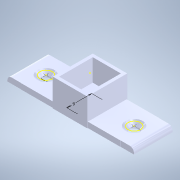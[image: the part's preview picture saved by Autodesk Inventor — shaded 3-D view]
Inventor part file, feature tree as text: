
AUTODESK INVENTOR PART (.ipt)
format: ipt  version: 2021 (Build 250183000, 183)  size: 252,928 bytes
history: mixed  units: in
note: dims shown in document units (in); Inventor stores cm internally (conversion verified against a paired STEP export)
features: sketch x12, extrude x7, hole x2, reference x2, other x2, fillet x1, projected_geometry x1, mirror x1, imported_body x1
ambient origin geometry x8: Origin, YZ Plane, XZ Plane, XY Plane, X Axis, Y Axis, Z Axis, Center Point
bodies: Solid1 (imported_parasolid)
feature tree (29):
  extrude  "Extrusion1"  Depth=0.315in
  sketch  "Sketch2"  dims[d3=0.1339in d4=0.2362in d5=0.248in d6=0.0787in d7=90.0deg d8=0.315in d9=0.0in d14=0.0039in]
  hole  "Hole1"  [1 undecoded]
  sketch  "Sketch4"  dims[d17=0.3937in d18=0.0in d20=0.5512in]
  extrude  "Extrusion3"  Depth=0.5512in
  extrude  "Extrusion4"  Depth=0.3937in TaperAngle=0.0deg
  fillet  "Fillet3"  Radius=0.0591in
  extrude  "Extrusion5"  Depth=0.3937in TaperAngle=0.0deg
  extrude  "Extrusion6"  Depth=0.4921in
  extrude  "Extrusion7"  Depth=0.4803in
  extrude  "Extrusion8"  Depth=0.315in
  sketch  "Sketch12"
  hole  "Hole2"  [1 undecoded]
  sketch  "Sketch1"  dims[d0=0.3937in d1=0.0in]
  reference  "Reference1"
  reference  "Reference2"
  sketch  "Sketch3"  dims[d15=1.8071in d16=0.5551in]
  sketch  "Sketch6"  dims[d21=0.1969in d22=0.3937in d23=0.0in d24=0.0591in]
  sketch  "Sketch7"  dims[d25=0.3937in d26=0.0in d27=0.3937in d28=0.0in]
  sketch  "Sketch8"  dims[d29=0.5709in d30=0.4921in]
  projected_geometry  "Projected Loop2"
  sketch  "Sketch9"  dims[d31=0.3937in d32=0.0in d33=0.4803in]
  sketch  "Sketch10"  dims[d34=0.315in d35=0.0in d36=0.3543in]
  sketch  "Sketch11"  dims[d37=0.0709in d38=0.2362in d39=0.1417in d40=0.0787in d41=90.0deg d42=0.315in d43=0.0in]
  sketch  "Sketch13"
  mirror  "Mirror1"
  other  "assy_gic_kinematic_2d_robot_arm_MK1_v2.iam"
  other  "base_bearing_holder_v1:1"
  imported_body  NMx_Import_Brep_tag  [imported B-rep: ~38 faces, bbox_mm=[45.9, 10.0, 14.5]]
note: 2 required parameter values undecoded (feature->parameter linkage not recoverable at this tier; creation-order binding heuristic only, values carry confidence <= 0.55)
